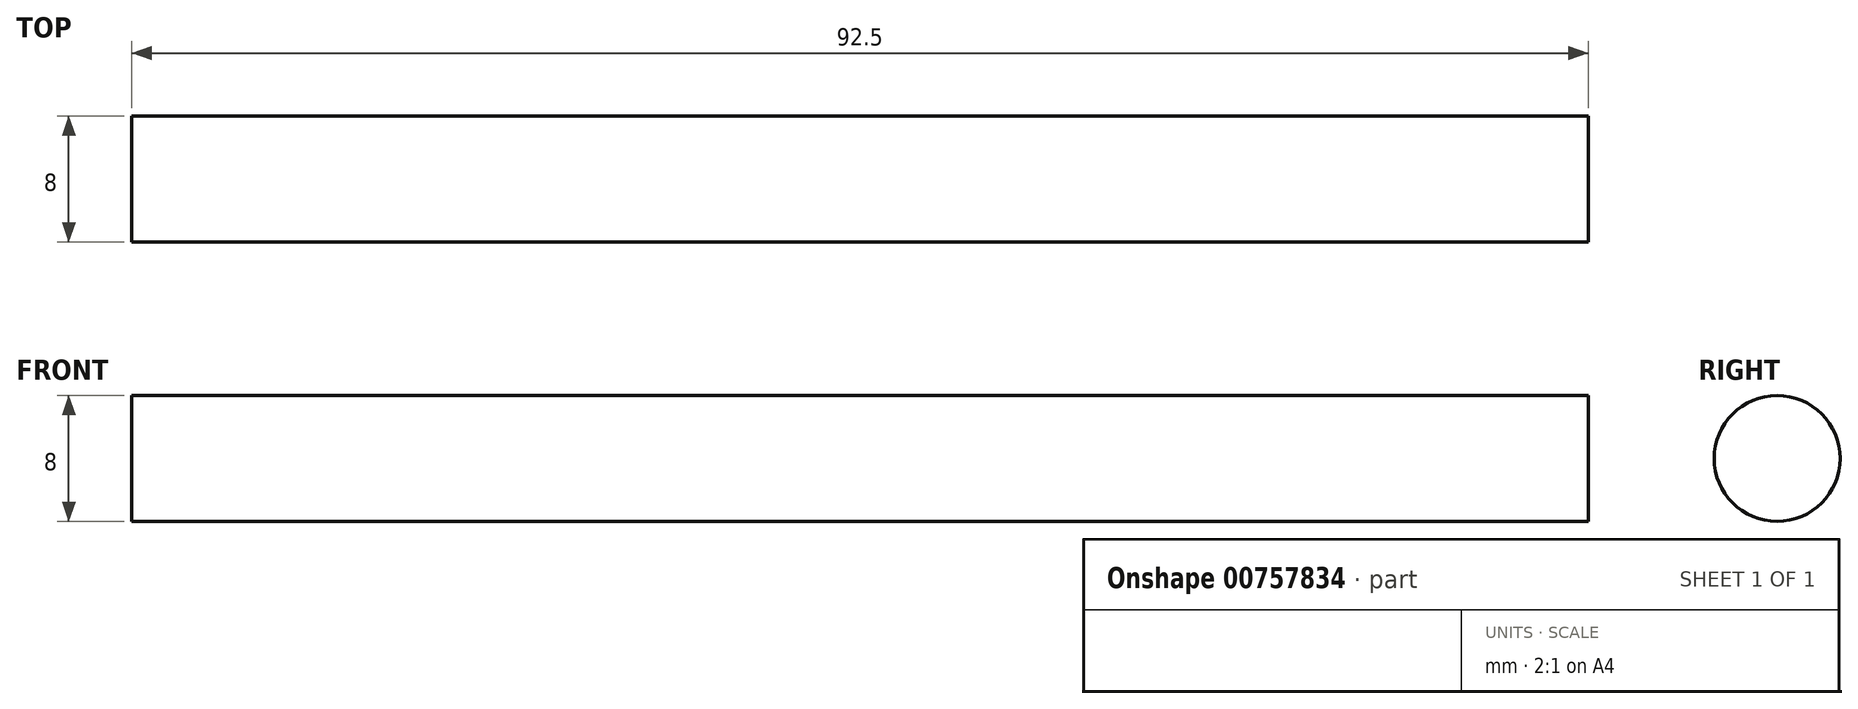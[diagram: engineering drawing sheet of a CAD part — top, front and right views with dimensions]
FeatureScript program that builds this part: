
annotation { "Feature Type Name" : "Feature", "Feature Type Description" : "" }
export const myFeature = defineFeature(function(context is Context, id is Id, definition is map)
    precondition{}
    {
        {
            var Q0;
            Q0=qCreatedBy(makeId("Right.planeOp"),FACE);
            var sketch = newSketch(context, id + "F0", { "sketchPlane" : qUnion([Q0])});
            skCircle(sketch, "E0", {"center": v(0, 0) * mm, "radius": 4 * mm});
            skSolve(sketch);
        }
        {
            var Q0;
            Q0 = qSketchRegion(id + "F0", true);
            extrude(context, id + "F1", {"entities" : qUnion([Q0]), "depth" : 92.5 * mm, "offsetDistance" : 25 * mm});
        }
    });
